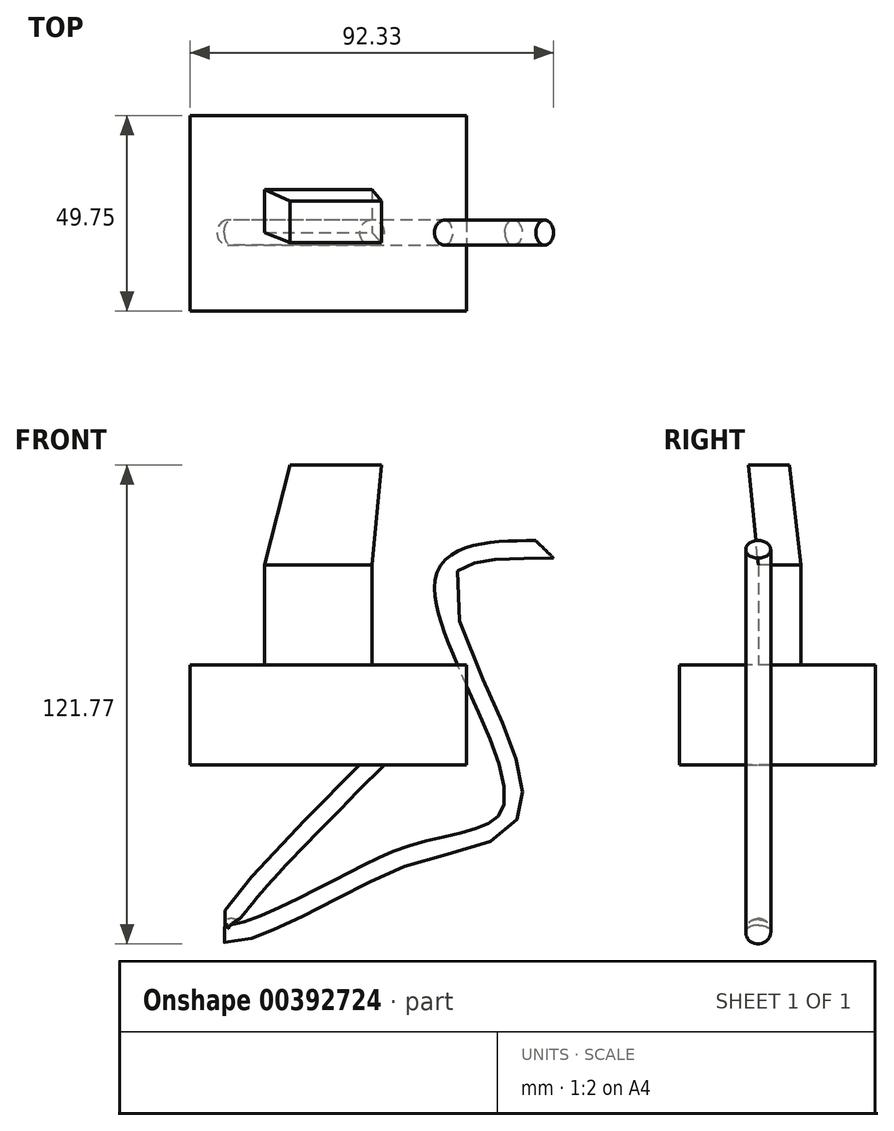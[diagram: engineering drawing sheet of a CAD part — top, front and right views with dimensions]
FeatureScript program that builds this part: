
annotation { "Feature Type Name" : "Feature", "Feature Type Description" : "" }
export const myFeature = defineFeature(function(context is Context, id is Id, definition is map)
    precondition{}
    {
        {
            var Q0;
            Q0=qCreatedBy(makeId("Top.planeOp"),FACE);
            var sketch = newSketch(context, id + "F0", { "sketchPlane" : qUnion([Q0])});
            skLineSegment(sketch, "E0.bottom", {"start": v(-90.28, 8.35) * mm, "end": v(77.59, 8.35) * mm});
            skLineSegment(sketch, "E0.top", {"start": v(-90.28, -26.16) * mm, "end": v(77.59, -26.16) * mm});
            skLineSegment(sketch, "E0.left", {"start": v(-90.28, 8.35) * mm, "end": v(-90.28, -26.16) * mm});
            skLineSegment(sketch, "E0.right", {"start": v(77.59, 8.35) * mm, "end": v(77.59, -26.16) * mm});
            skSolve(sketch);
        }
        {
            var Q0;
            Q0=qCreatedBy(makeId("Top.planeOp"),FACE);
            var sketch = newSketch(context, id + "F1", { "sketchPlane" : qUnion([Q0])});
            skLineSegment(sketch, "E1", {"start": v(-63.5, 36.47) * mm, "end": v(14.06, 62.89) * mm});
            skSolve(sketch);
        }
        {
            var Q0;
            Q0=qCreatedBy(makeId("Top.planeOp"),FACE);
            var sketch = newSketch(context, id + "F2", { "sketchPlane" : qUnion([Q0])});
            skCircle(sketch, "E2", {"center": v(0, 0) * mm, "radius": 3.18 * mm});
            skSolve(sketch);
        }
        {
            var Q0;
            Q0=qCreatedBy(makeId("Front.planeOp"),FACE);
            var sketch = newSketch(context, id + "F3", { "sketchPlane" : qUnion([Q0])});
            skFitSpline(sketch, "E3", {"points": [v(0, 0) * mm, v(-36.4, -42.39) * mm, v(-11.2, -32.72) * mm, v(13.97, -21.7) * mm, v(35.68, -9.74) * mm, v(18.46, 46.3) * mm, v(43.87, 54.71) * mm], "startDerivative": vector(-283.6, -284.9) * mm, "endDerivative": vector(249.37, 0.7) * mm});
            skSolve(sketch);
        }
        {
            var Q0;
            Q0=makeQuery(id+"F2.imprint","IMPRINT",FACE,{"disambiguationData":[TD([[makeQuery(id+"F2.imprint","IMPRINT",EDGE,{"derivedFrom":sQuery(id+"F2.wireOp",EDGE,"E2")}),1.0]])]});
            var Q1;
            Q1=sQuery(id+"F3.wireOp",EDGE,"E3");
            sweep(context, id + "F4", {"profiles" : qUnion([Q0]), "path" : qUnion([Q1])});
        }
        {
            var Q0;
            Q0=qCreatedBy(makeId("Top.planeOp"),FACE);
            var sketch = newSketch(context, id + "F5", { "sketchPlane" : qUnion([Q0])});
            skLineSegment(sketch, "E4.bottom", {"start": v(-46.2, 29.76) * mm, "end": v(24.04, 29.76) * mm});
            skLineSegment(sketch, "E4.top", {"start": v(-46.2, -19.99) * mm, "end": v(24.04, -19.99) * mm});
            skLineSegment(sketch, "E4.left", {"start": v(-46.2, 29.76) * mm, "end": v(-46.2, -19.99) * mm});
            skLineSegment(sketch, "E4.right", {"start": v(24.04, 29.76) * mm, "end": v(24.04, -19.99) * mm});
            skSolve(sketch);
        }
        {
            var Q0;
            Q0=makeQuery(id+"F5.imprint","IMPRINT",FACE,{"disambiguationData":[TD([[makeQuery(id+"F5.imprint","IMPRINT",EDGE,{"derivedFrom":sQuery(id+"F5.wireOp",EDGE,"E4.bottom")}),-1.0]])]});
            extrude(context, id + "F6", {"entities" : qUnion([Q0]), "depth" : 25.4 * mm});
        }
        {
            var Q0;
            Q0=makeQuery(id+"F6.opExtrude","CAP_FACE",FACE,{"disambiguationData":[OSD([sQuery(id+"F5.wireOp",EDGE,"E4.bottom"),sQuery(id+"F5.wireOp",EDGE,"E4.top"),sQuery(id+"F5.wireOp",EDGE,"E4.left"),sQuery(id+"F5.wireOp",EDGE,"E4.right")])],"isStart":false});
            var sketch = newSketch(context, id + "F7", { "sketchPlane" : qUnion([Q0])});
            skLineSegment(sketch, "E5.bottom", {"start": v(-27.24, 10.87) * mm, "end": v(0, 10.87) * mm});
            skLineSegment(sketch, "E5.top", {"start": v(-27.24, 0) * mm, "end": v(0, 0) * mm});
            skLineSegment(sketch, "E5.left", {"start": v(-27.24, 10.87) * mm, "end": v(-27.24, 0) * mm});
            skLineSegment(sketch, "E5.right", {"start": v(0, 10.87) * mm, "end": v(0, 0) * mm});
            skSolve(sketch);
        }
        {
            var Q0;
            Q0=makeQuery(id+"F7.imprint","IMPRINT",FACE,{"disambiguationData":[TD([[makeQuery(id+"F7.imprint","IMPRINT",EDGE,{"derivedFrom":sQuery(id+"F7.wireOp",EDGE,"E5.bottom")}),-1.0]])]});
            extrude(context, id + "F8", {"entities" : qUnion([Q0]), "operationType" : NewBodyOperationType.ADD, "depth" : 25.4 * mm});
        }
        {
            var Q0;
            Q0=qCreatedBy(makeId("Top.planeOp"),FACE);
            cPlane(context, id + "F9", {"entities" : qUnion([Q0]), "cplaneType" : CPlaneType.OFFSET, "offset" : 76.2 * mm, "width" : 152.4 * mm, "height" : 152.4 * mm});
        }
        {
            var Q0;
            Q0=qCreatedBy(id+"F9.planeOp",FACE);
            var sketch = newSketch(context, id + "F10", { "sketchPlane" : qUnion([Q0])});
            skLineSegment(sketch, "E6.bottom", {"start": v(-20.78, -2.52) * mm, "end": v(2.44, -2.52) * mm});
            skLineSegment(sketch, "E6.top", {"start": v(-20.78, 7.96) * mm, "end": v(2.44, 7.96) * mm});
            skLineSegment(sketch, "E6.left", {"start": v(-20.78, -2.52) * mm, "end": v(-20.78, 7.96) * mm});
            skLineSegment(sketch, "E6.right", {"start": v(2.44, -2.52) * mm, "end": v(2.44, 7.96) * mm});
            skSolve(sketch);
        }
        {
            var Q1;
            Q1=makeQuery(id+"F8.opExtrude","CAP_FACE",FACE,{"disambiguationData":[OSD([sQuery(id+"F7.wireOp",EDGE,"E5.bottom"),sQuery(id+"F7.wireOp",EDGE,"E5.top"),sQuery(id+"F7.wireOp",EDGE,"E5.left"),sQuery(id+"F7.wireOp",EDGE,"E5.right")])],"isStart":false});
            var Q2;
            Q2=makeQuery(id+"F10.imprint","IMPRINT",FACE,{"disambiguationData":[TD([[makeQuery(id+"F10.imprint","IMPRINT",EDGE,{"derivedFrom":sQuery(id+"F10.wireOp",EDGE,"E6.bottom")}),1.0]])]});
            loft(context, id + "F11", {"operationType" : NewBodyOperationType.ADD, "sheetProfilesArray" : [{ "sheetProfileEntities" : qUnion([Q1]) }, { "sheetProfileEntities" : qUnion([Q2]) }]});
        }
    });
